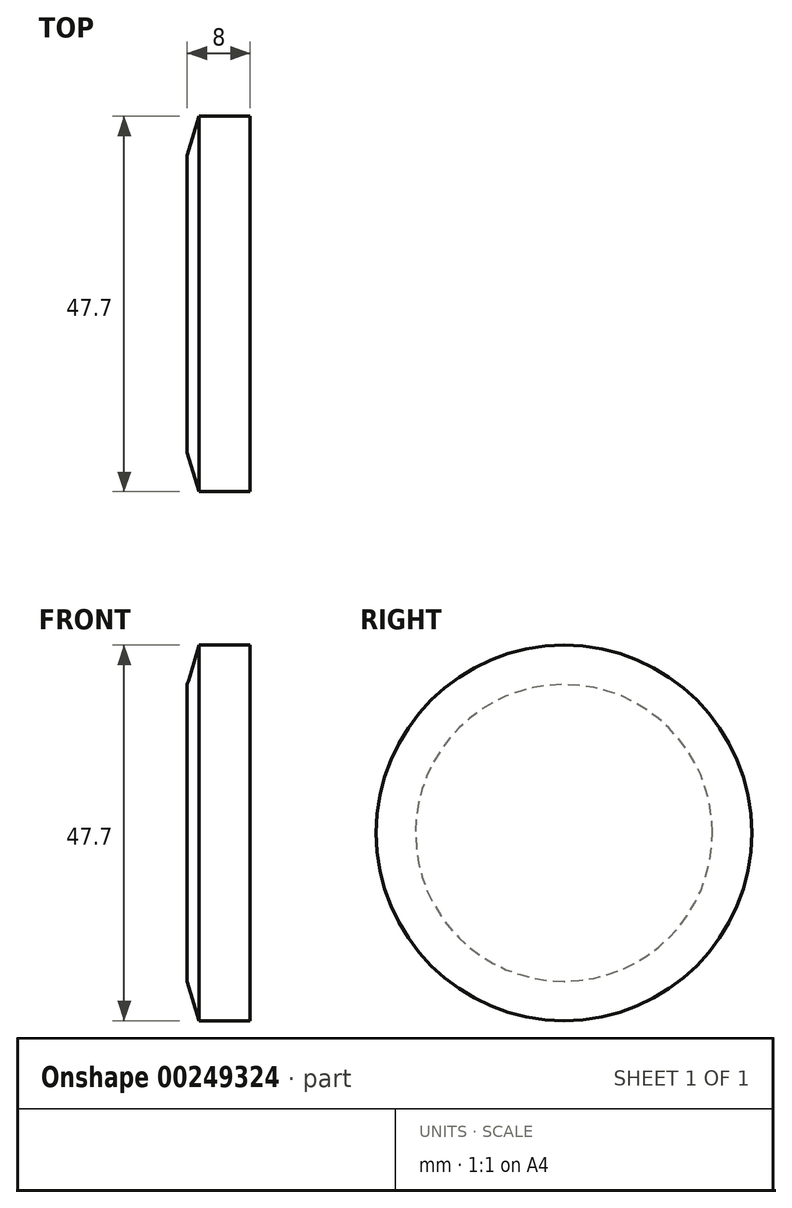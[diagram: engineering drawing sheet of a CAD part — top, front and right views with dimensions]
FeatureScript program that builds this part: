
annotation { "Feature Type Name" : "Feature", "Feature Type Description" : "" }
export const myFeature = defineFeature(function(context is Context, id is Id, definition is map)
    precondition{}
    {
        {
            var Q0;
            Q0=qCreatedBy(makeId("Front.planeOp"),FACE);
            var sketch = newSketch(context, id + "F0", { "sketchPlane" : qUnion([Q0])});
            skLineSegment(sketch, "E0", {"start": v(0, 0) * mm, "end": v(-8, 0) * mm});
            skLineSegment(sketch, "E1", {"start": v(0, 0) * mm, "end": v(0, 23.85) * mm});
            skLineSegment(sketch, "E2", {"start": v(0, 23.85) * mm, "end": v(-8, 23.85) * mm});
            skLineSegment(sketch, "E3", {"start": v(-8, 23.85) * mm, "end": v(-8, 0) * mm});
            skSolve(sketch);
        }
        {
            var Q0;
            Q0=makeQuery(id+"F0.imprint","IMPRINT",FACE,{"disambiguationData":[TD([[makeQuery(id+"F0.imprint","IMPRINT",EDGE,{"derivedFrom":sQuery(id+"F0.wireOp",EDGE,"E0")}),-1.0]])]});
            var Q1;
            Q1=sQuery(id+"F0.wireOp",EDGE,"E0");
            revolve(context, id + "F1", {"entities" : qUnion([Q0]), "axis" : qUnion([Q1]), "revolveType" : RevolveType.FULL});
        }
        {
            var Q0;
            Q0=makeQuery(id+"F1.opRevolve","SWEPT_EDGE",EDGE,{"disambiguationData":[OSD([sQuery(id+"F0.wireOp",EDGE,"E2"),sQuery(id+"F0.wireOp",EDGE,"E3")])]});
            chamfer(context, id + "F2", {"entities" : qUnion([Q0]), "chamferType" : ChamferType.TWO_OFFSETS, "width1" : 1.5 * mm, "oppositeDirection" : false, "width2" : 5 * mm, "tangentPropagation" : true});
        }
    });
